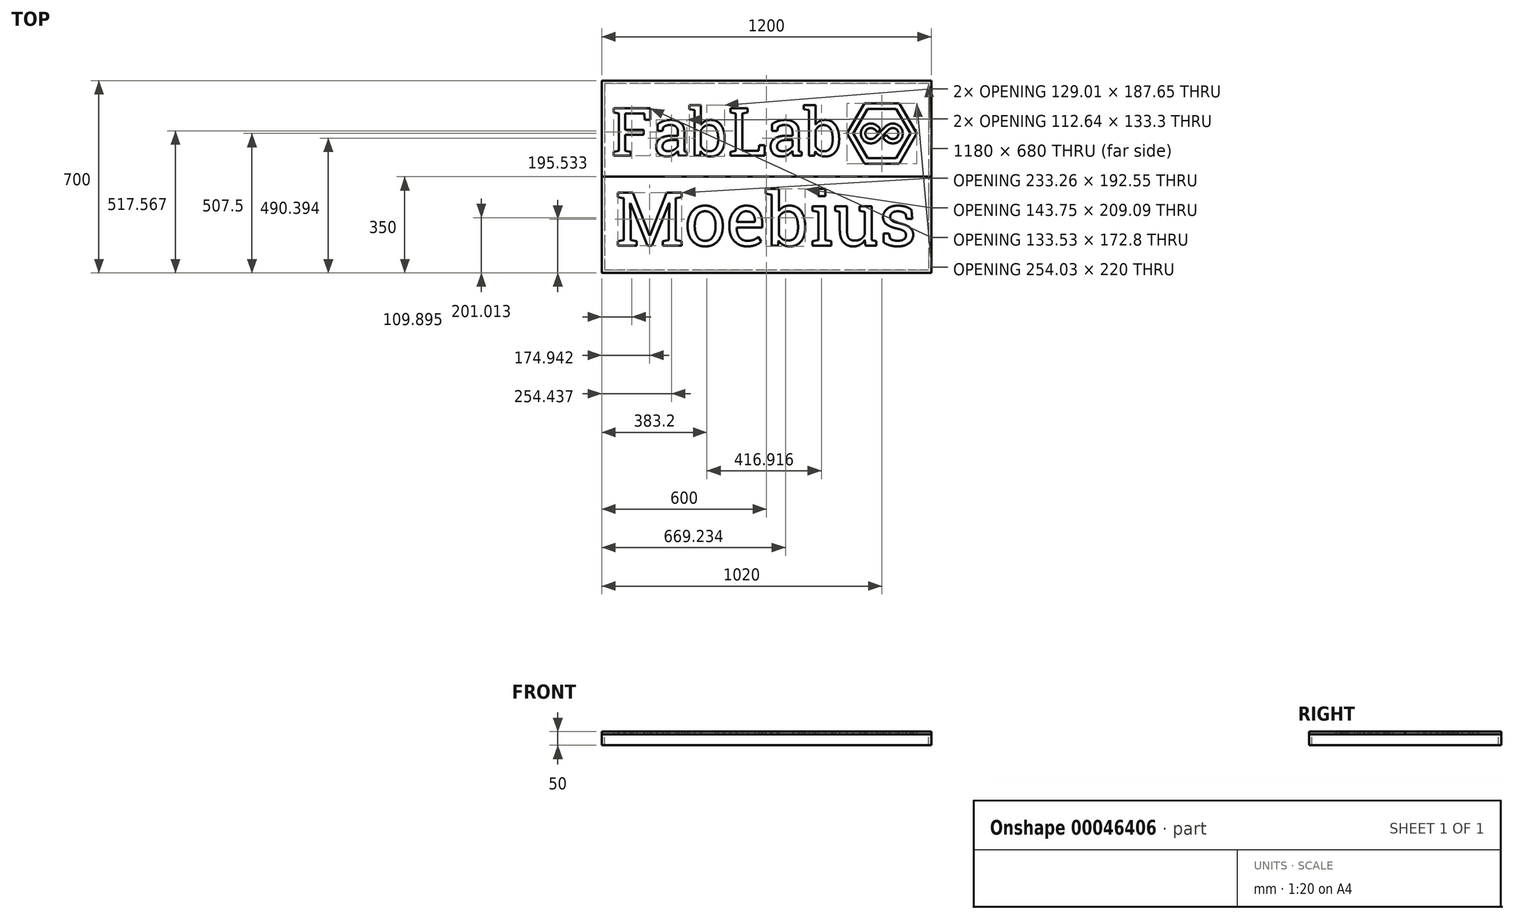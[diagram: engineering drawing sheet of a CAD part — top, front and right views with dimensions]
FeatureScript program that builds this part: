
annotation { "Feature Type Name" : "Feature", "Feature Type Description" : "" }
export const myFeature = defineFeature(function(context is Context, id is Id, definition is map)
    precondition{}
    {
        {
            var Q0;
            Q0=qCreatedBy(makeId("Top.planeOp"),FACE);
            var sketch = newSketch(context, id + "F0", { "sketchPlane" : qUnion([Q0])});
            skLineSegment(sketch, "E0.bottom", {"start": v(-600, 0) * mm, "end": v(600, 0) * mm});
            skLineSegment(sketch, "E0.top", {"start": v(-600, 350) * mm, "end": v(600, 350) * mm});
            skLineSegment(sketch, "E0.left", {"start": v(-600, 0) * mm, "end": v(-600, 350) * mm});
            skLineSegment(sketch, "E0.right", {"start": v(600, 0) * mm, "end": v(600, 350) * mm});
            skLineSegment(sketch, "E1.top", {"start": v(-600, -350) * mm, "end": v(600, -350) * mm});
            skLineSegment(sketch, "E1.left", {"start": v(-600, 0) * mm, "end": v(-600, -350) * mm});
            skLineSegment(sketch, "E1.right", {"start": v(600, 0) * mm, "end": v(600, -350) * mm});
            skSolve(sketch);
        }
        {
            var Q0;
            Q0=makeQuery(id+"F0.imprint","IMPRINT",FACE,{"disambiguationData":[TD([[makeQuery(id+"F0.imprint","IMPRINT",EDGE,{"derivedFrom":sQuery(id+"F0.wireOp",EDGE,"E0.bottom")}),1.0]])]});
            var sketch = newSketch(context, id + "F1", { "sketchPlane" : qUnion([Q0])});
            skText(sketch, "E2", { "text": "FabLab", "fontName": "RobotoSlab-Regular.ttf"});
            skLineSegment(sketch, "E3", {"start": v(-142.8, 6.25) * mm, "end": v(-142.8, 406.25) * mm, "construction": true});
            const initialGuessF1  = {"E2": [-0.5653, 0.07625, 1, 0, 0.175]};
            skSetInitialGuess(sketch, initialGuessF1);
            skSolve(sketch);
        }
        {
            var Q0;
            Q0=makeQuery(id+"F0.imprint","IMPRINT",FACE,{"disambiguationData":[TD([[makeQuery(id+"F0.imprint","IMPRINT",EDGE,{"derivedFrom":sQuery(id+"F0.wireOp",EDGE,"E0.bottom")}),-1.0]])]});
            var sketch = newSketch(context, id + "F2", { "sketchPlane" : qUnion([Q0])});
            skText(sketch, "E4", { "text": "Moebius", "fontName": "RobotoSlab-Regular.ttf"});
            skLineSegment(sketch, "E5", {"start": v(0, 0) * mm, "end": v(0, -400) * mm, "construction": true});
            const initialGuessF2  = {"E4": [-0.55108, -0.25074, 1, 0, 0.195]};
            skSetInitialGuess(sketch, initialGuessF2);
            skSolve(sketch);
        }
        {
            var Q0;
            Q0=makeQuery(id+"F0.imprint","IMPRINT",FACE,{"disambiguationData":[TD([[makeQuery(id+"F0.imprint","IMPRINT",EDGE,{"derivedFrom":sQuery(id+"F0.wireOp",EDGE,"E0.bottom")}),1.0]])]});
            extrude(context, id + "F3", {"entities" : qUnion([Q0]), "depth" : 10 * mm, "offsetDistance" : 25 * mm});
        }
        {
            var Q0;
            Q0=makeQuery(id+"F0.imprint","IMPRINT",FACE,{"disambiguationData":[TD([[makeQuery(id+"F0.imprint","IMPRINT",EDGE,{"derivedFrom":sQuery(id+"F0.wireOp",EDGE,"E0.bottom")}),-1.0]])]});
            extrude(context, id + "F4", {"entities" : qUnion([Q0]), "depth" : 10 * mm, "offsetDistance" : 25 * mm});
        }
        {
            var Q0;
            Q0 = qSketchRegion(id + "F1", true);
            extrude(context, id + "F5", {"entities" : qUnion([Q0]), "operationType" : NewBodyOperationType.REMOVE, "endBound" : BoundingType.THROUGH_ALL, "depth" : 25 * mm, "offsetDistance" : 25 * mm});
        }
        {
            var Q0;
            {var subQ0=sQuery(id+"F0.wireOp",EDGE,"E0.left");var subQ1=sQuery(id+"F0.wireOp",EDGE,"E0.top");var subQ2=sQuery(id+"F0.wireOp",EDGE,"E0.right");var subQ3=sQuery(id+"F0.wireOp",EDGE,"E0.bottom");Q0=makeQuery(id+"F5.boolean.opBoolean","SPLIT",FACE,{"disambiguationData":[TD([makeQuery(id+"F3.opExtrude","SWEPT_FACE",FACE,{"disambiguationData":[OSD([subQ3])]})])],"derivedFrom":makeQuery(id+"F3.opExtrude","CAP_FACE",FACE,{"disambiguationData":[OSD([subQ3,subQ1,subQ0,subQ2])],"isStart":false})});}
            var sketch = newSketch(context, id + "F6", { "sketchPlane" : qUnion([Q0])});
            skCircle(sketch, "E6.cCircle", {"center": v(420, 157.5) * mm, "radius": 90 * mm, "construction": true});
            skLineSegment(sketch, "E6.0", {"start": v(471.96, 247.5) * mm, "end": v(523.92, 157.5) * mm});
            skLineSegment(sketch, "E6.1", {"start": v(523.92, 157.5) * mm, "end": v(471.96, 67.5) * mm});
            skLineSegment(sketch, "E6.2", {"start": v(471.96, 67.5) * mm, "end": v(368.04, 67.5) * mm});
            skLineSegment(sketch, "E6.3", {"start": v(368.04, 67.5) * mm, "end": v(316.08, 157.5) * mm});
            skLineSegment(sketch, "E6.4", {"start": v(316.08, 157.5) * mm, "end": v(368.04, 247.5) * mm});
            skLineSegment(sketch, "E6.5", {"start": v(368.04, 247.5) * mm, "end": v(471.96, 247.5) * mm});
            skPoint(sketch, "E6.0.midPoint", {"position": v(497.94, 202.5) * mm});
            skPoint(sketch, "E7", {"position": v(440, 157.5) * mm});
            skLineSegment(sketch, "E8", {"start": v(420, 247.5) * mm, "end": v(420, 67.5) * mm, "construction": true});
            skPoint(sketch, "E9", {"position": v(460, 157.5) * mm});
            skPoint(sketch, "E10", {"position": v(440, 177.5) * mm});
            skLineSegment(sketch, "E11", {"start": v(420, 157.5) * mm, "end": v(440, 177.5) * mm});
            skArc(sketch, "E12", {"start": v(440, 177.5) * mm, "mid": v(488.28, 157.5) * mm, "end": v(440, 137.5) * mm});
            skLineSegment(sketch, "E13", {"start": v(440, 137.5) * mm, "end": v(430, 147.5) * mm});
            skPoint(sketch, "E14.MirrorP", {"position": v(400, 157.5) * mm});
            skLineSegment(sketch, "E15", {"start": v(420, 157.5) * mm, "end": v(400, 137.5) * mm});
            skPoint(sketch, "E16", {"position": v(380, 157.5) * mm});
            skArc(sketch, "E17", {"start": v(400, 137.5) * mm, "mid": v(351.72, 157.5) * mm, "end": v(400, 177.5) * mm});
            skLineSegment(sketch, "E18", {"start": v(400, 177.5) * mm, "end": v(410, 167.5) * mm});
            skLineSegment(sketch, "E19.0", {"start": v(394.34, 171.84) * mm, "end": v(404.34, 161.84) * mm});
            skArc(sketch, "E19.1", {"start": v(394.34, 143.16) * mm, "mid": v(359.72, 157.5) * mm, "end": v(394.34, 171.84) * mm});
            skLineSegment(sketch, "E19.2", {"start": v(434.34, 131.84) * mm, "end": v(424.34, 141.84) * mm});
            skArc(sketch, "E19.3", {"start": v(434.34, 183.16) * mm, "mid": v(496.28, 157.5) * mm, "end": v(434.34, 131.84) * mm});
            skLineSegment(sketch, "E19.4", {"start": v(411.31, 160.13) * mm, "end": v(434.34, 183.16) * mm});
            skLineSegment(sketch, "E19.5", {"start": v(411.31, 160.13) * mm, "end": v(394.34, 143.16) * mm});
            skLineSegment(sketch, "E20", {"start": v(316.08, 157.5) * mm, "end": v(523.92, 157.5) * mm, "construction": true});
            skLineSegment(sketch, "E21.0", {"start": v(405.66, 183.16) * mm, "end": v(415.66, 173.16) * mm});
            skArc(sketch, "E21.1", {"start": v(405.66, 131.84) * mm, "mid": v(343.72, 157.5) * mm, "end": v(405.66, 183.16) * mm});
            skLineSegment(sketch, "E21.2", {"start": v(445.66, 143.16) * mm, "end": v(435.66, 153.16) * mm});
            skArc(sketch, "E21.3", {"start": v(445.66, 171.84) * mm, "mid": v(480.28, 157.5) * mm, "end": v(445.66, 143.16) * mm});
            skLineSegment(sketch, "E21.4", {"start": v(422.63, 148.81) * mm, "end": v(445.66, 171.84) * mm});
            skLineSegment(sketch, "E21.5", {"start": v(422.63, 148.81) * mm, "end": v(405.66, 131.84) * mm});
            skLineSegment(sketch, "E22", {"start": v(424.34, 141.84) * mm, "end": v(435.66, 153.16) * mm});
            skLineSegment(sketch, "E23", {"start": v(404.34, 161.84) * mm, "end": v(415.66, 173.16) * mm});
            skLineSegment(sketch, "E24.0", {"start": v(292.98, 157.5) * mm, "end": v(356.5, 267.5) * mm});
            skLineSegment(sketch, "E24.1", {"start": v(483.5, 267.5) * mm, "end": v(547.02, 157.5) * mm});
            skLineSegment(sketch, "E24.2", {"start": v(547.02, 157.5) * mm, "end": v(483.5, 47.5) * mm});
            skLineSegment(sketch, "E24.3", {"start": v(356.5, 267.5) * mm, "end": v(483.5, 267.5) * mm});
            skLineSegment(sketch, "E24.4", {"start": v(483.5, 47.5) * mm, "end": v(356.5, 47.5) * mm});
            skLineSegment(sketch, "E24.5", {"start": v(356.5, 47.5) * mm, "end": v(292.98, 157.5) * mm});
            skSolve(sketch);
        }
        {
            var Q0;
            Q0=makeQuery(id+"F6.imprint","IMPRINT",FACE,{"disambiguationData":[TD([[makeQuery(id+"F6.imprint","IMPRINT",EDGE,{"derivedFrom":sQuery(id+"F6.wireOp",EDGE,"E6.0")}),1.0]])]});
            var Q1;
            Q1=makeQuery(id+"F6.imprint","IMPRINT",FACE,{"disambiguationData":[TD([[makeQuery(id+"F6.imprint","IMPRINT",EDGE,{"derivedFrom":sQuery(id+"F6.wireOp",EDGE,"E11")}),-1.0]])]});
            var Q2;
            Q2=makeQuery(id+"F6.imprint","IMPRINT",FACE,{"disambiguationData":[TD([[makeQuery(id+"F6.imprint","IMPRINT",EDGE,{"derivedFrom":sQuery(id+"F6.wireOp",EDGE,"E11")}),1.0]])]});
            var Q3;
            {var subQ1=sQuery(id+"F6.wireOp",EDGE,"E19.0");Q3=makeQuery(id+"F6.imprint","IMPRINT",FACE,{"disambiguationData":[TD([[makeQuery(id+"F6.imprint","IMPRINT",EDGE,{"derivedFrom":subQ1}),1.0]])]});}
            extrude(context, id + "F7", {"entities" : qUnion([Q0, Q1, Q2, Q3]), "operationType" : NewBodyOperationType.REMOVE, "endBound" : BoundingType.THROUGH_ALL, "oppositeDirection" : true, "depth" : 25 * mm, "offsetDistance" : 25 * mm});
        }
        {
            var Q0;
            Q0 = qSketchRegion(id + "F2", true);
            extrude(context, id + "F8", {"entities" : qUnion([Q0]), "operationType" : NewBodyOperationType.REMOVE, "endBound" : BoundingType.THROUGH_ALL, "depth" : 25 * mm, "offsetDistance" : 25 * mm});
        }
        {
            var Q0;
            Q0=qCreatedBy(makeId("Top.planeOp"),FACE);
            var sketch = newSketch(context, id + "F9", { "sketchPlane" : qUnion([Q0])});
            skLineSegment(sketch, "E25.bottom", {"start": v(600, 350) * mm, "end": v(-600, 350) * mm});
            skLineSegment(sketch, "E25.top", {"start": v(600, -350) * mm, "end": v(-600, -350) * mm});
            skLineSegment(sketch, "E25.left", {"start": v(600, 350) * mm, "end": v(600, -350) * mm});
            skLineSegment(sketch, "E25.right", {"start": v(-600, 350) * mm, "end": v(-600, -350) * mm});
            skPoint(sketch, "E25.middle", {"position": v(0, 0) * mm});
            skLineSegment(sketch, "E26.bottom", {"start": v(590, 340) * mm, "end": v(-590, 340) * mm});
            skLineSegment(sketch, "E26.top", {"start": v(590, -340) * mm, "end": v(-590, -340) * mm});
            skLineSegment(sketch, "E26.left", {"start": v(590, 340) * mm, "end": v(590, -340) * mm});
            skLineSegment(sketch, "E26.right", {"start": v(-590, 340) * mm, "end": v(-590, -340) * mm});
            skSolve(sketch);
        }
        {
            var Q0;
            Q0=makeQuery(id+"F9.imprint","IMPRINT",FACE,{"disambiguationData":[TD([[makeQuery(id+"F9.imprint","IMPRINT",EDGE,{"derivedFrom":sQuery(id+"F9.wireOp",EDGE,"E25.bottom")}),1.0]])]});
            extrude(context, id + "F10", {"entities" : qUnion([Q0]), "oppositeDirection" : true, "depth" : 40 * mm, "offsetDistance" : 25 * mm});
        }
    });
